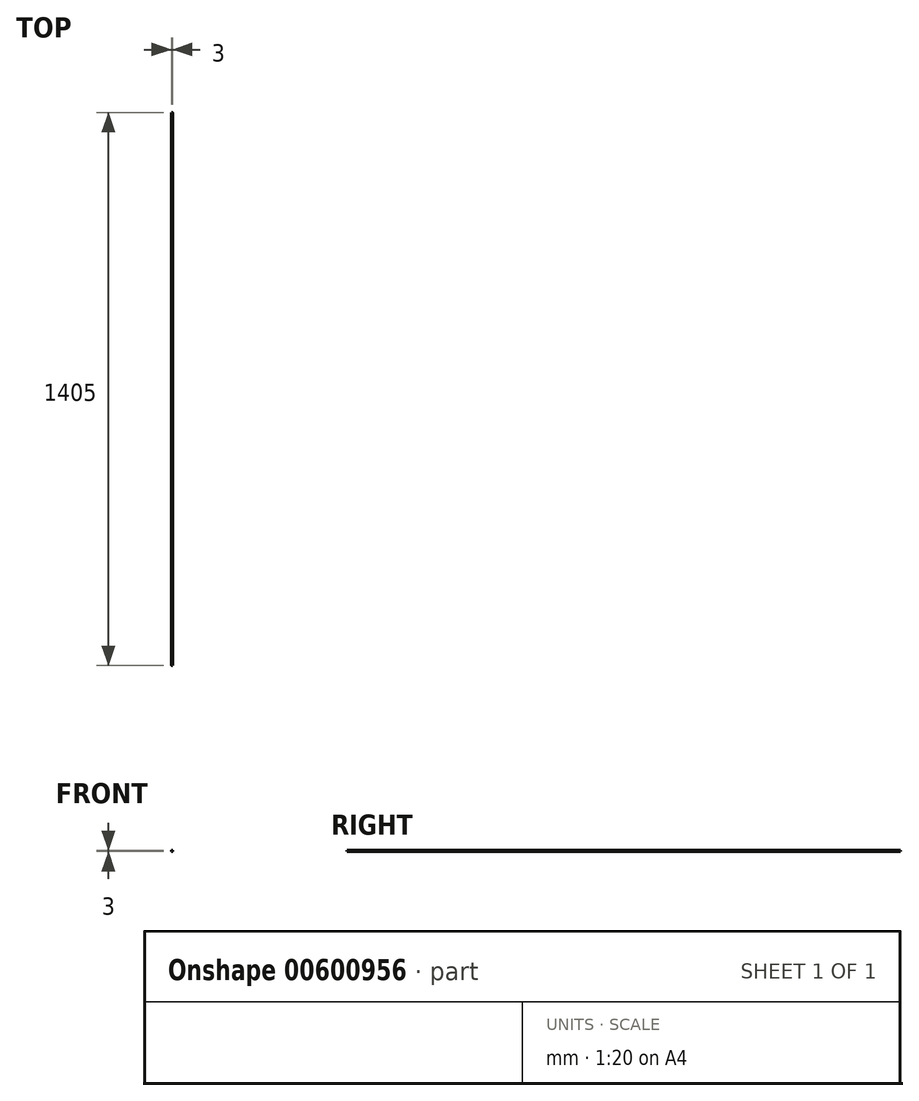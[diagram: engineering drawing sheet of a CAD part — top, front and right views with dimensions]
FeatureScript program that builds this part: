
annotation { "Feature Type Name" : "Feature", "Feature Type Description" : "" }
export const myFeature = defineFeature(function(context is Context, id is Id, definition is map)
    precondition{}
    {
        {
            var Q0;
            Q0=qCreatedBy(makeId("Front.planeOp"),FACE);
            var sketch = newSketch(context, id + "F0", { "sketchPlane" : qUnion([Q0])});
            skCircle(sketch, "E0", {"center": v(0, 0) * mm, "radius": 1.5 * mm});
            skSolve(sketch);
        }
        {
            var Q0;
            Q0=makeQuery(id+"F0.imprint","IMPRINT",FACE,{"disambiguationData":[TD([[makeQuery(id+"F0.imprint","IMPRINT",EDGE,{"derivedFrom":sQuery(id+"F0.wireOp",EDGE,"E0")}),1.0]])]});
            extrude(context, id + "F1", {"entities" : qUnion([Q0]), "depth" : 1405 * mm, "offsetDistance" : 25 * mm});
        }
    });
